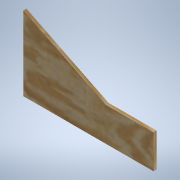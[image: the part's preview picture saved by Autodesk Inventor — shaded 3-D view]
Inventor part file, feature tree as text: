
AUTODESK INVENTOR PART (.ipt)
format: ipt  version: 2021.1 (Build 251245000, 245)  size: 110,080 bytes
history: native  units: mm
features: extrude x1, sketch x1
ambient origin geometry x8: Origin, YZ Plane, XZ Plane, XY Plane, X Axis, Y Axis, Z Axis, Center Point
bodies: Solid1 (feature_tree)
feature tree (2):
  extrude  "Extrusion1"  [1 undecoded]
  sketch  "Sketch1"  dims[d1=6.35mm d2=0.0mm]
note: 1 required parameter value undecoded (feature->parameter linkage not recoverable at this tier; creation-order binding heuristic only, values carry confidence <= 0.55)
